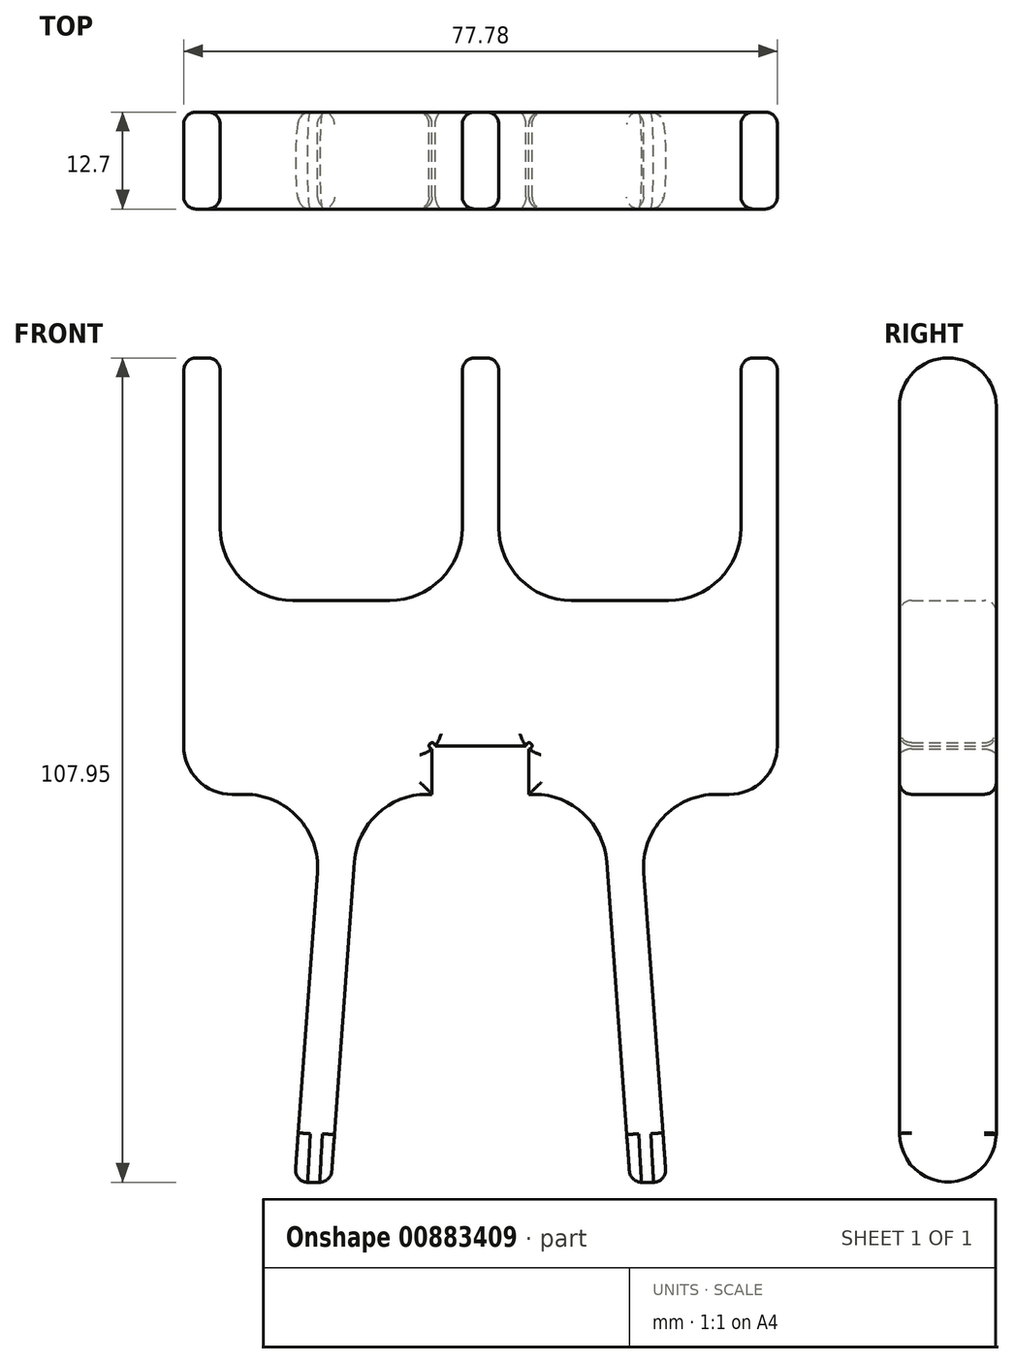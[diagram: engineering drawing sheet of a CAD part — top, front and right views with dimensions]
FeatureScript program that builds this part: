
annotation { "Feature Type Name" : "Feature", "Feature Type Description" : "" }
export const myFeature = defineFeature(function(context is Context, id is Id, definition is map)
    precondition{}
    {
        {
            var Q0;
            Q0=qCreatedBy(makeId("Front.planeOp"),FACE);
            var sketch = newSketch(context, id + "F0", { "sketchPlane" : qUnion([Q0])});
            skLineSegment(sketch, "E0", {"start": v(-6.35, 0) * mm, "end": v(-7.02, 0) * mm});
            skLineSegment(sketch, "E1", {"start": v(-16.52, -8.83) * mm, "end": v(-19.6, -50.8) * mm});
            skLineSegment(sketch, "E2", {"start": v(-19.6, -50.8) * mm, "end": v(-24.37, -50.8) * mm});
            skLineSegment(sketch, "E3", {"start": v(-24.37, -50.8) * mm, "end": v(-21.39, -10.22) * mm});
            skLineSegment(sketch, "E4", {"start": v(-30.89, 0) * mm, "end": v(-38.9, 0) * mm});
            skLineSegment(sketch, "E5", {"start": v(-38.9, 0) * mm, "end": v(-38.9, 57.15) * mm});
            skLineSegment(sketch, "E6", {"start": v(-38.9, 57.15) * mm, "end": v(-34.13, 57.15) * mm});
            skLineSegment(sketch, "E7", {"start": v(-34.13, 57.15) * mm, "end": v(-34.13, 34.92) * mm});
            skLineSegment(sketch, "E8", {"start": v(-24.6, 25.4) * mm, "end": v(-11.9, 25.4) * mm});
            skLineSegment(sketch, "E9", {"start": v(0, 6.35) * mm, "end": v(0, 6.35) * mm});
            skLineSegment(sketch, "E10", {"start": v(0, 0) * mm, "end": v(0, -50.8) * mm, "construction": true});
            skLineSegment(sketch, "E11", {"start": v(0, 57.15) * mm, "end": v(-2.38, 57.15) * mm});
            skLineSegment(sketch, "E12", {"start": v(-2.38, 57.15) * mm, "end": v(-2.38, 34.93) * mm});
            skPoint(sketch, "E13.visualSharp", {"position": v(-15.88, 0) * mm});
            skArc(sketch, "E13.filletArc", {"start": v(-7.02, 0) * mm, "mid": v(-13.5, -2.55) * mm, "end": v(-16.52, -8.83) * mm});
            skPoint(sketch, "E14.visualSharp", {"position": v(-34.13, 25.4) * mm});
            skArc(sketch, "E14.filletArc", {"start": v(-34.13, 34.92) * mm, "mid": v(-31.34, 28.19) * mm, "end": v(-24.6, 25.4) * mm});
            skPoint(sketch, "E15.newPointA", {"position": v(-2.38, 25.4) * mm});
            skPoint(sketch, "E15.newPointB", {"position": v(0, 25.4) * mm});
            skArc(sketch, "E15.filletArc", {"start": v(-11.9, 25.4) * mm, "mid": v(-5.17, 28.19) * mm, "end": v(-2.38, 34.93) * mm});
            skPoint(sketch, "E16.visualSharp", {"position": v(-20.64, 0) * mm});
            skArc(sketch, "E16.filletArc", {"start": v(-21.39, -10.22) * mm, "mid": v(-23.91, -3.04) * mm, "end": v(-30.89, 0) * mm});
            skPoint(sketch, "E17.visualSharp", {"position": v(-38.9, 0) * mm});
            skLineSegment(sketch, "E18", {"start": v(-6.35, 0) * mm, "end": v(-6.35, 6.35) * mm});
            skLineSegment(sketch, "E19", {"start": v(-6.35, 6.35) * mm, "end": v(0, 6.35) * mm});
            skCircle(sketch, "E20", {"center": v(-6.35, 6.35) * mm, "radius": 0.4 * mm});
            skPoint(sketch, "E21.orphan", {"position": v(0, 0) * mm});
            skLineSegment(sketch, "E22", {"start": v(0, 0) * mm, "end": v(0, 57.15) * mm, "construction": true});
            skLineSegment(sketch, "E23.MirrorCS", {"start": v(0, 57.15) * mm, "end": v(2.38, 57.15) * mm});
            skLineSegment(sketch, "E24.MirrorCS", {"start": v(2.38, 57.15) * mm, "end": v(2.38, 34.93) * mm});
            skArc(sketch, "E25.MirrorCS", {"start": v(11.9, 25.4) * mm, "mid": v(5.17, 28.19) * mm, "end": v(2.38, 34.93) * mm});
            skLineSegment(sketch, "E26.MirrorCS", {"start": v(24.6, 25.4) * mm, "end": v(11.9, 25.4) * mm});
            skArc(sketch, "E27.MirrorCS", {"start": v(34.13, 34.92) * mm, "mid": v(31.34, 28.19) * mm, "end": v(24.6, 25.4) * mm});
            skLineSegment(sketch, "E28.MirrorCS", {"start": v(34.13, 57.15) * mm, "end": v(34.13, 34.92) * mm});
            skLineSegment(sketch, "E29.MirrorCS", {"start": v(38.9, 57.15) * mm, "end": v(34.13, 57.15) * mm});
            skLineSegment(sketch, "E30.MirrorCS", {"start": v(38.9, 0) * mm, "end": v(38.9, 57.15) * mm});
            skLineSegment(sketch, "E31.MirrorCS", {"start": v(30.89, 0) * mm, "end": v(38.9, 0) * mm});
            skArc(sketch, "E32.MirrorCS", {"start": v(21.39, -10.22) * mm, "mid": v(23.91, -3.04) * mm, "end": v(30.89, 0) * mm});
            skLineSegment(sketch, "E33.MirrorCS", {"start": v(24.37, -50.8) * mm, "end": v(21.39, -10.22) * mm});
            skLineSegment(sketch, "E34.MirrorCS", {"start": v(19.6, -50.8) * mm, "end": v(24.37, -50.8) * mm});
            skLineSegment(sketch, "E35.MirrorCS", {"start": v(16.52, -8.83) * mm, "end": v(19.6, -50.8) * mm});
            skArc(sketch, "E36.MirrorCS", {"start": v(7.02, 0) * mm, "mid": v(13.5, -2.55) * mm, "end": v(16.52, -8.83) * mm});
            skLineSegment(sketch, "E37.MirrorCS", {"start": v(6.35, 0) * mm, "end": v(7.02, 0) * mm});
            skLineSegment(sketch, "E38.MirrorCS", {"start": v(6.35, 0) * mm, "end": v(6.35, 6.35) * mm});
            skLineSegment(sketch, "E39.MirrorCS", {"start": v(6.35, 6.35) * mm, "end": v(0, 6.35) * mm});
            skCircle(sketch, "E40.MirrorC", {"center": v(6.35, 6.35) * mm, "radius": 0.4 * mm});
            skSolve(sketch);
        }
        {
            var Q0;
            Q0=makeQuery(id+"F0.imprint","IMPRINT",FACE,{"disambiguationData":[TD([[makeQuery(id+"F0.imprint","IMPRINT",EDGE,{"derivedFrom":sQuery(id+"F0.wireOp",EDGE,"E0")}),-1.0]])]});
            var Q1;
            Q1=makeQuery(id+"F0.imprint","IMPRINT",FACE,{"disambiguationData":[TD([[makeQuery(id+"F0.imprint","IMPRINT",EDGE,{"derivedFrom":sQuery(id+"F0.wireOp",EDGE,"E9")}),1.0]])]});
            extrude(context, id + "F1", {"entities" : qUnion([Q0, Q1]), "depth" : 12.7 * mm, "offsetDistance" : 25.4 * mm});
        }
        {
            var Q0;
            Q0=makeQuery(id+"F1.opExtrude","CAP_EDGE",EDGE,{"disambiguationData":[OSD([sQuery(id+"F0.wireOp",EDGE,"E6")])],"isStart":false});
            var Q1;
            Q1=makeQuery(id+"F1.opExtrude","CAP_EDGE",EDGE,{"disambiguationData":[OSD([sQuery(id+"F0.wireOp",EDGE,"E11"),sQuery(id+"F0.wireOp",EDGE,"E23.MirrorCS")])],"isStart":false});
            var Q2;
            Q2=makeQuery(id+"F1.opExtrude","CAP_EDGE",EDGE,{"disambiguationData":[OSD([sQuery(id+"F0.wireOp",EDGE,"E29.MirrorCS")])],"isStart":false});
            var Q3;
            Q3=makeQuery(id+"F1.opExtrude","CAP_EDGE",EDGE,{"disambiguationData":[OSD([sQuery(id+"F0.wireOp",EDGE,"E6")])],"isStart":true});
            var Q4;
            Q4=makeQuery(id+"F1.opExtrude","CAP_EDGE",EDGE,{"disambiguationData":[OSD([sQuery(id+"F0.wireOp",EDGE,"E11"),sQuery(id+"F0.wireOp",EDGE,"E23.MirrorCS")])],"isStart":true});
            var Q5;
            Q5=makeQuery(id+"F1.opExtrude","CAP_EDGE",EDGE,{"disambiguationData":[OSD([sQuery(id+"F0.wireOp",EDGE,"E29.MirrorCS")])],"isStart":true});
            var Q6;
            Q6=makeQuery(id+"F1.opExtrude","CAP_EDGE",EDGE,{"disambiguationData":[OSD([sQuery(id+"F0.wireOp",EDGE,"E2")])],"isStart":true});
            var Q7;
            Q7=makeQuery(id+"F1.opExtrude","CAP_EDGE",EDGE,{"disambiguationData":[OSD([sQuery(id+"F0.wireOp",EDGE,"E34.MirrorCS")])],"isStart":true});
            var Q8;
            Q8=makeQuery(id+"F1.opExtrude","CAP_EDGE",EDGE,{"disambiguationData":[OSD([sQuery(id+"F0.wireOp",EDGE,"E34.MirrorCS")])],"isStart":false});
            var Q9;
            Q9=makeQuery(id+"F1.opExtrude","CAP_EDGE",EDGE,{"disambiguationData":[OSD([sQuery(id+"F0.wireOp",EDGE,"E2")])],"isStart":false});
            var Q10;
            Q10=makeQuery(id+"F1.opExtrude","SWEPT_EDGE",EDGE,{"disambiguationData":[OSD([sQuery(id+"F0.wireOp",EDGE,"E4"),sQuery(id+"F0.wireOp",EDGE,"E5")])]});
            var Q11;
            Q11=makeQuery(id+"F1.opExtrude","SWEPT_EDGE",EDGE,{"disambiguationData":[OSD([sQuery(id+"F0.wireOp",EDGE,"E30.MirrorCS"),sQuery(id+"F0.wireOp",EDGE,"E31.MirrorCS")])]});
            fillet(context, id + "F2", {"entities" : qUnion([Q0, Q1, Q2, Q3, Q4, Q5, Q6, Q7, Q8, Q9, Q10, Q11]), "radius" : 6.35 * mm, "tangentPropagation" : true, "allowEdgeOverflow" : false});
        }
        {
            var Q0;
            Q0=makeQuery(id+"F1.opExtrude","CAP_FACE",FACE,{"disambiguationData":[OSD([sQuery(id+"F0.wireOp",EDGE,"E0"),sQuery(id+"F0.wireOp",EDGE,"E1"),sQuery(id+"F0.wireOp",EDGE,"E2"),sQuery(id+"F0.wireOp",EDGE,"E3"),sQuery(id+"F0.wireOp",EDGE,"E4"),sQuery(id+"F0.wireOp",EDGE,"E5"),sQuery(id+"F0.wireOp",EDGE,"E6"),sQuery(id+"F0.wireOp",EDGE,"E7"),sQuery(id+"F0.wireOp",EDGE,"E8"),sQuery(id+"F0.wireOp",EDGE,"E11"),sQuery(id+"F0.wireOp",EDGE,"E12"),sQuery(id+"F0.wireOp",EDGE,"E13.filletArc"),sQuery(id+"F0.wireOp",EDGE,"E14.filletArc"),sQuery(id+"F0.wireOp",EDGE,"E15.filletArc"),sQuery(id+"F0.wireOp",EDGE,"E16.filletArc"),sQuery(id+"F0.wireOp",EDGE,"E18"),sQuery(id+"F0.wireOp",EDGE,"E19"),sQuery(id+"F0.wireOp",EDGE,"E20"),sQuery(id+"F0.wireOp",EDGE,"E23.MirrorCS"),sQuery(id+"F0.wireOp",EDGE,"E24.MirrorCS"),sQuery(id+"F0.wireOp",EDGE,"E25.MirrorCS"),sQuery(id+"F0.wireOp",EDGE,"E26.MirrorCS"),sQuery(id+"F0.wireOp",EDGE,"E27.MirrorCS"),sQuery(id+"F0.wireOp",EDGE,"E28.MirrorCS"),sQuery(id+"F0.wireOp",EDGE,"E29.MirrorCS"),sQuery(id+"F0.wireOp",EDGE,"E30.MirrorCS"),sQuery(id+"F0.wireOp",EDGE,"E31.MirrorCS"),sQuery(id+"F0.wireOp",EDGE,"E32.MirrorCS"),sQuery(id+"F0.wireOp",EDGE,"E33.MirrorCS"),sQuery(id+"F0.wireOp",EDGE,"E34.MirrorCS"),sQuery(id+"F0.wireOp",EDGE,"E35.MirrorCS"),sQuery(id+"F0.wireOp",EDGE,"E36.MirrorCS"),sQuery(id+"F0.wireOp",EDGE,"E37.MirrorCS"),sQuery(id+"F0.wireOp",EDGE,"E38.MirrorCS"),sQuery(id+"F0.wireOp",EDGE,"E39.MirrorCS"),sQuery(id+"F0.wireOp",EDGE,"E40.MirrorC")])],"isStart":false});
            var Q1;
            Q1=makeQuery(id+"F1.opExtrude","CAP_FACE",FACE,{"disambiguationData":[OSD([sQuery(id+"F0.wireOp",EDGE,"E0"),sQuery(id+"F0.wireOp",EDGE,"E1"),sQuery(id+"F0.wireOp",EDGE,"E2"),sQuery(id+"F0.wireOp",EDGE,"E3"),sQuery(id+"F0.wireOp",EDGE,"E4"),sQuery(id+"F0.wireOp",EDGE,"E5"),sQuery(id+"F0.wireOp",EDGE,"E6"),sQuery(id+"F0.wireOp",EDGE,"E7"),sQuery(id+"F0.wireOp",EDGE,"E8"),sQuery(id+"F0.wireOp",EDGE,"E11"),sQuery(id+"F0.wireOp",EDGE,"E12"),sQuery(id+"F0.wireOp",EDGE,"E13.filletArc"),sQuery(id+"F0.wireOp",EDGE,"E14.filletArc"),sQuery(id+"F0.wireOp",EDGE,"E15.filletArc"),sQuery(id+"F0.wireOp",EDGE,"E16.filletArc"),sQuery(id+"F0.wireOp",EDGE,"E18"),sQuery(id+"F0.wireOp",EDGE,"E19"),sQuery(id+"F0.wireOp",EDGE,"E20"),sQuery(id+"F0.wireOp",EDGE,"E23.MirrorCS"),sQuery(id+"F0.wireOp",EDGE,"E24.MirrorCS"),sQuery(id+"F0.wireOp",EDGE,"E25.MirrorCS"),sQuery(id+"F0.wireOp",EDGE,"E26.MirrorCS"),sQuery(id+"F0.wireOp",EDGE,"E27.MirrorCS"),sQuery(id+"F0.wireOp",EDGE,"E28.MirrorCS"),sQuery(id+"F0.wireOp",EDGE,"E29.MirrorCS"),sQuery(id+"F0.wireOp",EDGE,"E30.MirrorCS"),sQuery(id+"F0.wireOp",EDGE,"E31.MirrorCS"),sQuery(id+"F0.wireOp",EDGE,"E32.MirrorCS"),sQuery(id+"F0.wireOp",EDGE,"E33.MirrorCS"),sQuery(id+"F0.wireOp",EDGE,"E34.MirrorCS"),sQuery(id+"F0.wireOp",EDGE,"E35.MirrorCS"),sQuery(id+"F0.wireOp",EDGE,"E36.MirrorCS"),sQuery(id+"F0.wireOp",EDGE,"E37.MirrorCS"),sQuery(id+"F0.wireOp",EDGE,"E38.MirrorCS"),sQuery(id+"F0.wireOp",EDGE,"E39.MirrorCS"),sQuery(id+"F0.wireOp",EDGE,"E40.MirrorC")])],"isStart":true});
            fillet(context, id + "F3", {"entities" : qUnion([Q0, Q1]), "radius" : 1.59 * mm, "tangentPropagation" : true, "allowEdgeOverflow" : false});
        }
    });
